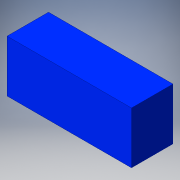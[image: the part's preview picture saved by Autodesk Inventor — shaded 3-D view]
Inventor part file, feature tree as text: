
AUTODESK INVENTOR PART (.ipt)
format: ipt  version: 2016 (Build 200138000, 138)  size: 91,136 bytes
history: native  units: in
note: dims shown in document units (in); Inventor stores cm internally (conversion verified against a paired STEP export)
features: extrude x1, sketch x1
ambient origin geometry x8: Origin, YZ Plane, XZ Plane, XY Plane, X Axis, Y Axis, Z Axis, Center Point
bodies: Solid1 (feature_tree)
feature tree (2):
  extrude  "Extrusion1"  Depth=1.25in
  sketch  "Sketch1"  dims[d0=3.0in d1=1.25in d2=1.0in d3=0.0in]
